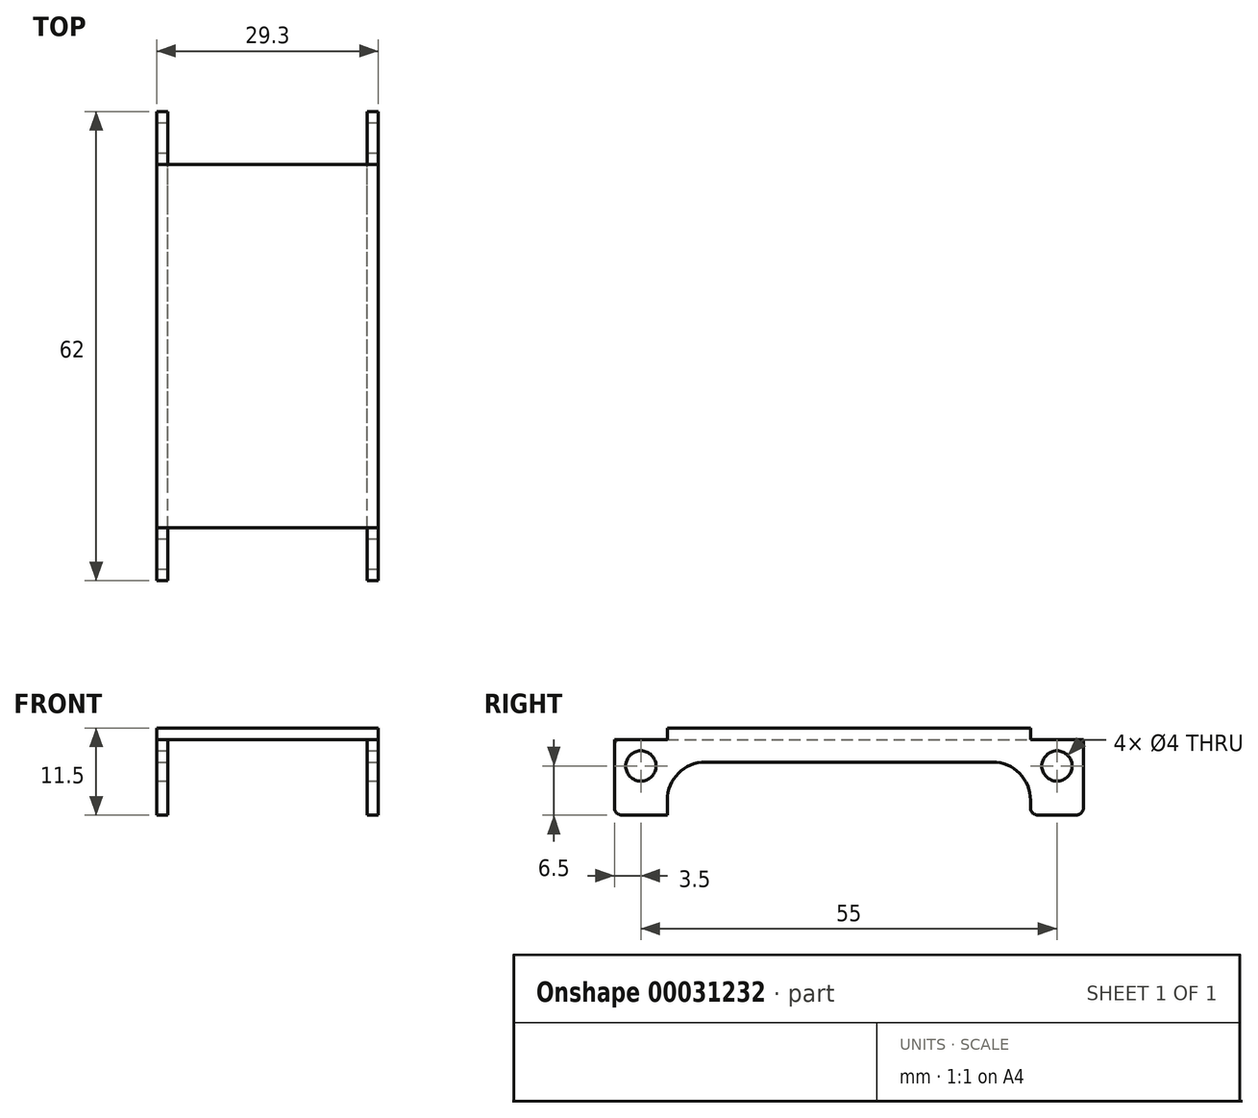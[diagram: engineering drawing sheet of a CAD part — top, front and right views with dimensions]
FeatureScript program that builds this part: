
annotation { "Feature Type Name" : "Feature", "Feature Type Description" : "" }
export const myFeature = defineFeature(function(context is Context, id is Id, definition is map)
    precondition{}
    {
        {
            var Q0;
            Q0=qCreatedBy(makeId("Front.planeOp"),FACE);
            var sketch = newSketch(context, id + "F0", { "sketchPlane" : qUnion([Q0])});
            skLineSegment(sketch, "E0.bottom", {"start": v(0, 0) * mm, "end": v(1.5, 0) * mm});
            skLineSegment(sketch, "E0.top", {"start": v(0, 11.5) * mm, "end": v(29.3, 11.5) * mm});
            skLineSegment(sketch, "E0.left", {"start": v(0, 0) * mm, "end": v(0, 11.5) * mm});
            skLineSegment(sketch, "E0.right", {"start": v(29.3, 0) * mm, "end": v(29.3, 11.5) * mm});
            skLineSegment(sketch, "E1.top", {"start": v(1.5, 10) * mm, "end": v(27.8, 10) * mm});
            skLineSegment(sketch, "E1.left", {"start": v(1.5, 0) * mm, "end": v(1.5, 10) * mm});
            skLineSegment(sketch, "E1.right", {"start": v(27.8, 0) * mm, "end": v(27.8, 10) * mm});
            skLineSegment(sketch, "E2.trimOffspring", {"start": v(27.8, 0) * mm, "end": v(29.3, 0) * mm});
            skSolve(sketch);
        }
        {
            var Q0;
            Q0 = qSketchRegion(id + "F0", true);
            extrude(context, id + "F1", {"entities" : qUnion([Q0]), "depth" : 62 * mm});
        }
        {
            var Q0;
            Q0=makeQuery(id+"F1.opExtrude","SWEPT_FACE",FACE,{"disambiguationData":[OSD([sQuery(id+"F0.wireOp",EDGE,"E0.right")])]});
            var sketch = newSketch(context, id + "F2", { "sketchPlane" : qUnion([Q0])});
            skCircle(sketch, "E3", {"center": v(-58.5, 6.5) * mm, "radius": 2 * mm});
            skCircle(sketch, "E4", {"center": v(-3.5, 6.5) * mm, "radius": 2 * mm});
            skSolve(sketch);
        }
        {
            var Q0;
            Q0 = qSketchRegion(id + "F2", true);
            extrude(context, id + "F3", {"entities" : qUnion([Q0]), "operationType" : NewBodyOperationType.REMOVE, "endBound" : BoundingType.THROUGH_ALL, "oppositeDirection" : true, "depth" : 25 * mm});
        }
        {
            var Q0;
            Q0=makeQuery(id+"F1.opExtrude","SWEPT_FACE",FACE,{"disambiguationData":[OSD([sQuery(id+"F0.wireOp",EDGE,"E0.right")])]});
            var sketch = newSketch(context, id + "F4", { "sketchPlane" : qUnion([Q0])});
            skPoint(sketch, "E5", {"position": v(-58.5, 6.5) * mm});
            skLineSegment(sketch, "E6.bottom", {"start": v(-7, 0) * mm, "end": v(-55, 0) * mm});
            skLineSegment(sketch, "E6.top", {"start": v(-7, 7) * mm, "end": v(-55, 7) * mm});
            skLineSegment(sketch, "E6.left", {"start": v(-7, 0) * mm, "end": v(-7, 7) * mm});
            skLineSegment(sketch, "E6.right", {"start": v(-55, 0) * mm, "end": v(-55, 7) * mm});
            skPoint(sketch, "E7", {"position": v(-3.5, 6.5) * mm});
            skSolve(sketch);
        }
        {
            var Q0;
            Q0 = qSketchRegion(id + "F4", true);
            extrude(context, id + "F5", {"entities" : qUnion([Q0]), "operationType" : NewBodyOperationType.REMOVE, "endBound" : BoundingType.THROUGH_ALL, "oppositeDirection" : true, "depth" : 25 * mm});
        }
        {
            var Q0;
            Q0=makeQuery(id+"F1.opExtrude","CAP_EDGE",EDGE,{"disambiguationData":[OSD([sQuery(id+"F0.wireOp",EDGE,"E2.trimOffspring")])],"isStart":false});
            var Q1;
            Q1=makeQuery(id+"F5.boolean.opBoolean","COPY",EDGE,{"disambiguationData":[OD(0.0)],"derivedFrom":makeQuery(id+"F5.opExtrude","SWEPT_EDGE",EDGE,{"disambiguationData":[OSD([sQuery(id+"F0.wireOp",EDGE,"E0.right"),sQuery(id+"F0.wireOp",EDGE,"E2.trimOffspring"),sQuery(id+"F4.wireOp",EDGE,"E6.bottom"),sQuery(id+"F4.wireOp",EDGE,"E6.right")])]})});
            var Q2;
            Q2=makeQuery(id+"F1.opExtrude","CAP_EDGE",EDGE,{"disambiguationData":[OSD([sQuery(id+"F0.wireOp",EDGE,"E0.bottom")])],"isStart":false});
            var Q3;
            Q3=makeQuery(id+"F5.boolean.opBoolean","COPY",EDGE,{"disambiguationData":[OD(1.0)],"derivedFrom":makeQuery(id+"F5.opExtrude","SWEPT_EDGE",EDGE,{"disambiguationData":[OSD([sQuery(id+"F0.wireOp",EDGE,"E0.right"),sQuery(id+"F0.wireOp",EDGE,"E2.trimOffspring"),sQuery(id+"F4.wireOp",EDGE,"E6.bottom"),sQuery(id+"F4.wireOp",EDGE,"E6.right")])]})});
            var Q4;
            Q4=makeQuery(id+"F1.opExtrude","CAP_EDGE",EDGE,{"disambiguationData":[OSD([sQuery(id+"F0.wireOp",EDGE,"E2.trimOffspring")])],"isStart":true});
            var Q5;
            Q5=makeQuery(id+"F5.boolean.opBoolean","COPY",EDGE,{"disambiguationData":[OD(0.0)],"derivedFrom":makeQuery(id+"F5.opExtrude","SWEPT_EDGE",EDGE,{"disambiguationData":[OSD([sQuery(id+"F0.wireOp",EDGE,"E0.right"),sQuery(id+"F0.wireOp",EDGE,"E2.trimOffspring"),sQuery(id+"F4.wireOp",EDGE,"E6.bottom"),sQuery(id+"F4.wireOp",EDGE,"E6.left")])]})});
            var Q6;
            Q6=makeQuery(id+"F5.boolean.opBoolean","COPY",EDGE,{"disambiguationData":[OD(1.0)],"derivedFrom":makeQuery(id+"F5.opExtrude","SWEPT_EDGE",EDGE,{"disambiguationData":[OSD([sQuery(id+"F0.wireOp",EDGE,"E0.right"),sQuery(id+"F0.wireOp",EDGE,"E2.trimOffspring"),sQuery(id+"F4.wireOp",EDGE,"E6.bottom"),sQuery(id+"F4.wireOp",EDGE,"E6.left")])]})});
            var Q7;
            Q7=makeQuery(id+"F1.opExtrude","CAP_EDGE",EDGE,{"disambiguationData":[OSD([sQuery(id+"F0.wireOp",EDGE,"E0.bottom")])],"isStart":true});
            fillet(context, id + "F6", {"entities" : qUnion([Q0, Q1, Q2, Q3, Q4, Q5, Q6, Q7]), "radius" : 1 * mm, "tangentPropagation" : true, "allowEdgeOverflow" : false});
        }
        {
            var Q0;
            Q0=makeQuery(id+"F5.boolean.opBoolean","COPY",EDGE,{"disambiguationData":[OD(0.0)],"derivedFrom":makeQuery(id+"F5.opExtrude","SWEPT_EDGE",EDGE,{"disambiguationData":[OSD([sQuery(id+"F4.wireOp",EDGE,"E6.top"),sQuery(id+"F4.wireOp",EDGE,"E6.left")])]})});
            var Q1;
            Q1=makeQuery(id+"F5.boolean.opBoolean","COPY",EDGE,{"disambiguationData":[OD(1.0)],"derivedFrom":makeQuery(id+"F5.opExtrude","SWEPT_EDGE",EDGE,{"disambiguationData":[OSD([sQuery(id+"F4.wireOp",EDGE,"E6.top"),sQuery(id+"F4.wireOp",EDGE,"E6.left")])]})});
            var Q2;
            Q2=makeQuery(id+"F5.boolean.opBoolean","COPY",EDGE,{"disambiguationData":[OD(0.0)],"derivedFrom":makeQuery(id+"F5.opExtrude","SWEPT_EDGE",EDGE,{"disambiguationData":[OSD([sQuery(id+"F4.wireOp",EDGE,"E6.top"),sQuery(id+"F4.wireOp",EDGE,"E6.right")])]})});
            var Q3;
            Q3=makeQuery(id+"F5.boolean.opBoolean","COPY",EDGE,{"disambiguationData":[OD(1.0)],"derivedFrom":makeQuery(id+"F5.opExtrude","SWEPT_EDGE",EDGE,{"disambiguationData":[OSD([sQuery(id+"F4.wireOp",EDGE,"E6.top"),sQuery(id+"F4.wireOp",EDGE,"E6.right")])]})});
            fillet(context, id + "F7", {"entities" : qUnion([Q0, Q1, Q2, Q3]), "radius" : 5 * mm, "tangentPropagation" : true, "allowEdgeOverflow" : false});
        }
        {
            var Q0;
            Q0=makeQuery(id+"F1.opExtrude","SWEPT_FACE",FACE,{"disambiguationData":[OSD([sQuery(id+"F0.wireOp",EDGE,"E0.top")])]});
            var sketch = newSketch(context, id + "F8", { "sketchPlane" : qUnion([Q0])});
            skLineSegment(sketch, "E8", {"start": v(0, -31) * mm, "end": v(29.3, -31) * mm, "construction": true});
            skLineSegment(sketch, "E9.bottom", {"start": v(29.3, -62) * mm, "end": v(0, -62) * mm});
            skLineSegment(sketch, "E9.top", {"start": v(29.3, -55) * mm, "end": v(0, -55) * mm});
            skLineSegment(sketch, "E9.left", {"start": v(29.3, -62) * mm, "end": v(29.3, -55) * mm});
            skLineSegment(sketch, "E9.right", {"start": v(0, -62) * mm, "end": v(0, -55) * mm});
            skLineSegment(sketch, "E10.MirrorCS", {"start": v(0, 0) * mm, "end": v(0, -7) * mm});
            skLineSegment(sketch, "E11.MirrorCS", {"start": v(29.3, 0) * mm, "end": v(0, 0) * mm});
            skLineSegment(sketch, "E12.MirrorCS", {"start": v(29.3, 0) * mm, "end": v(29.3, -7) * mm});
            skLineSegment(sketch, "E13.MirrorCS", {"start": v(29.3, -7) * mm, "end": v(0, -7) * mm});
            skSolve(sketch);
        }
        {
            var Q0;
            Q0 = qSketchRegion(id + "F8", true);
            extrude(context, id + "F9", {"entities" : qUnion([Q0]), "operationType" : NewBodyOperationType.REMOVE, "oppositeDirection" : true, "depth" : 1.5 * mm});
        }
        {
            var Q0;
            Q0=makeQuery(id+"F9.boolean.opBoolean","COPY",EDGE,{"disambiguationData":[OD(0.0)],"derivedFrom":makeQuery(id+"F9.opExtrude","CAP_EDGE",EDGE,{"disambiguationData":[OSD([sQuery(id+"F8.wireOp",EDGE,"E9.bottom")])],"isStart":false})});
            var Q1;
            Q1=makeQuery(id+"F9.boolean.opBoolean","COPY",EDGE,{"disambiguationData":[OD(1.0)],"derivedFrom":makeQuery(id+"F9.opExtrude","CAP_EDGE",EDGE,{"disambiguationData":[OSD([sQuery(id+"F8.wireOp",EDGE,"E9.bottom")])],"isStart":false})});
            var Q2;
            Q2=makeQuery(id+"F9.boolean.opBoolean","COPY",EDGE,{"disambiguationData":[OD(0.0)],"derivedFrom":makeQuery(id+"F9.opExtrude","CAP_EDGE",EDGE,{"disambiguationData":[OSD([sQuery(id+"F8.wireOp",EDGE,"E11.MirrorCS")])],"isStart":false})});
            var Q3;
            Q3=makeQuery(id+"F9.boolean.opBoolean","COPY",EDGE,{"disambiguationData":[OD(1.0)],"derivedFrom":makeQuery(id+"F9.opExtrude","CAP_EDGE",EDGE,{"disambiguationData":[OSD([sQuery(id+"F8.wireOp",EDGE,"E11.MirrorCS")])],"isStart":false})});
            fillet(context, id + "F10", {"entities" : qUnion([Q0, Q1, Q2, Q3]), "radius" : 1 * mm, "tangentPropagation" : true, "allowEdgeOverflow" : false});
        }
    });
